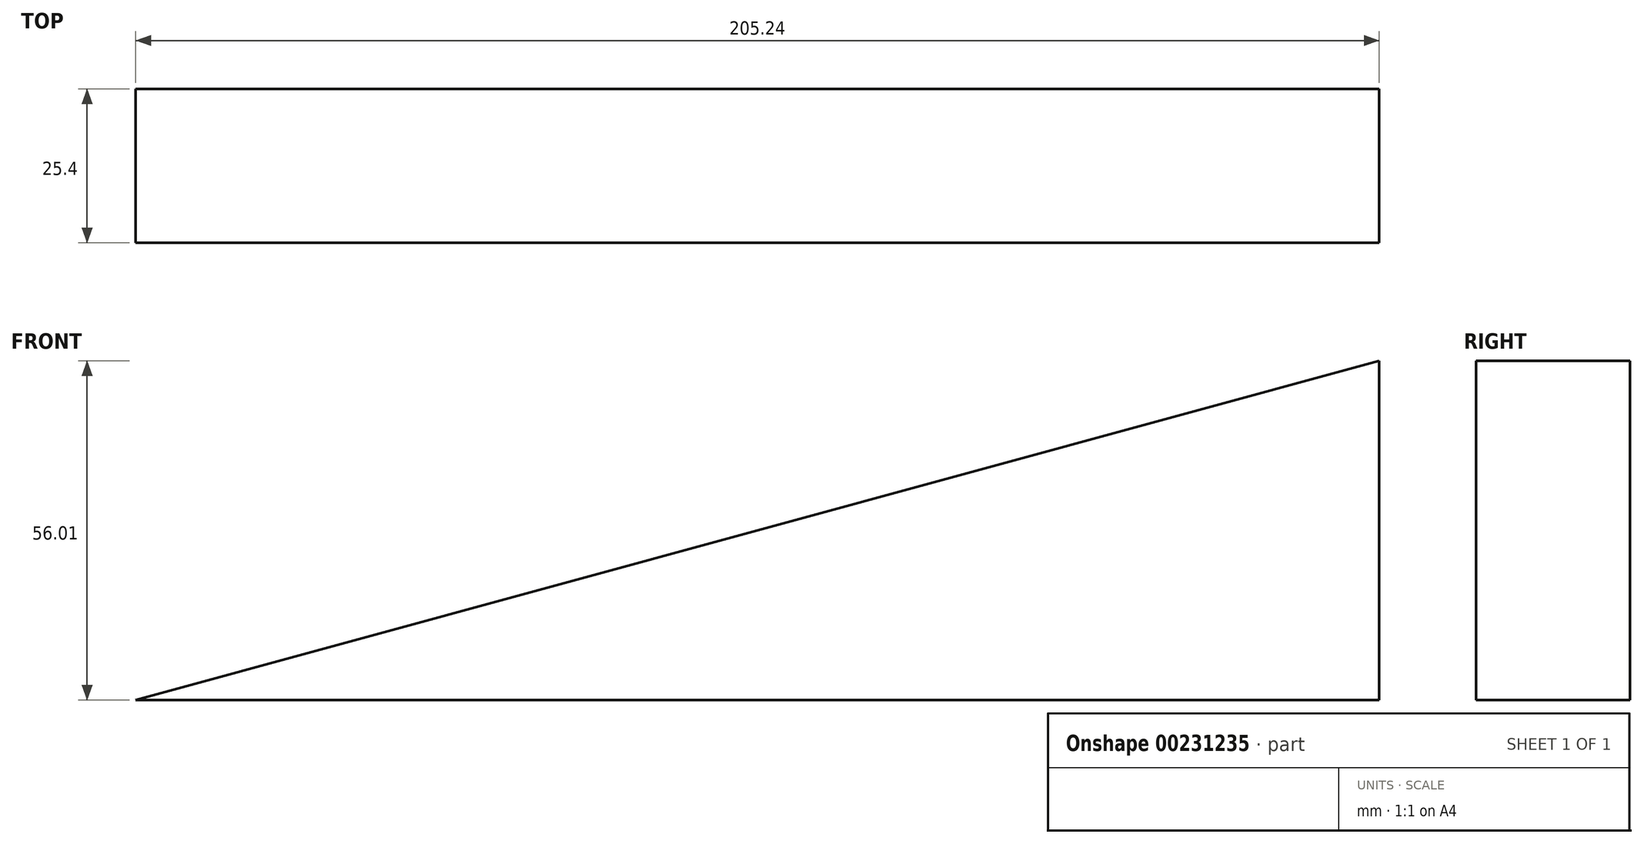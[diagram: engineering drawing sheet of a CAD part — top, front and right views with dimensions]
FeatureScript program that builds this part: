
annotation { "Feature Type Name" : "Feature", "Feature Type Description" : "" }
export const myFeature = defineFeature(function(context is Context, id is Id, definition is map)
    precondition{}
    {
        {
            var Q0;
            Q0=qCreatedBy(makeId("Front.planeOp"),FACE);
            var sketch = newSketch(context, id + "F0", { "sketchPlane" : qUnion([Q0])});
            skLineSegment(sketch, "E0", {"start": v(-99.84, 0) * mm, "end": v(105.4, 0) * mm});
            skLineSegment(sketch, "E1", {"start": v(105.4, 0) * mm, "end": v(105.4, 56) * mm});
            skLineSegment(sketch, "E2", {"start": v(105.4, 56) * mm, "end": v(-99.84, 0) * mm});
            skSolve(sketch);
        }
        {
            var Q0;
            Q0 = qSketchRegion(id + "F0", true);
            extrude(context, id + "F1", {"entities" : qUnion([Q0]), "depth" : 25.4 * mm});
        }
    });
